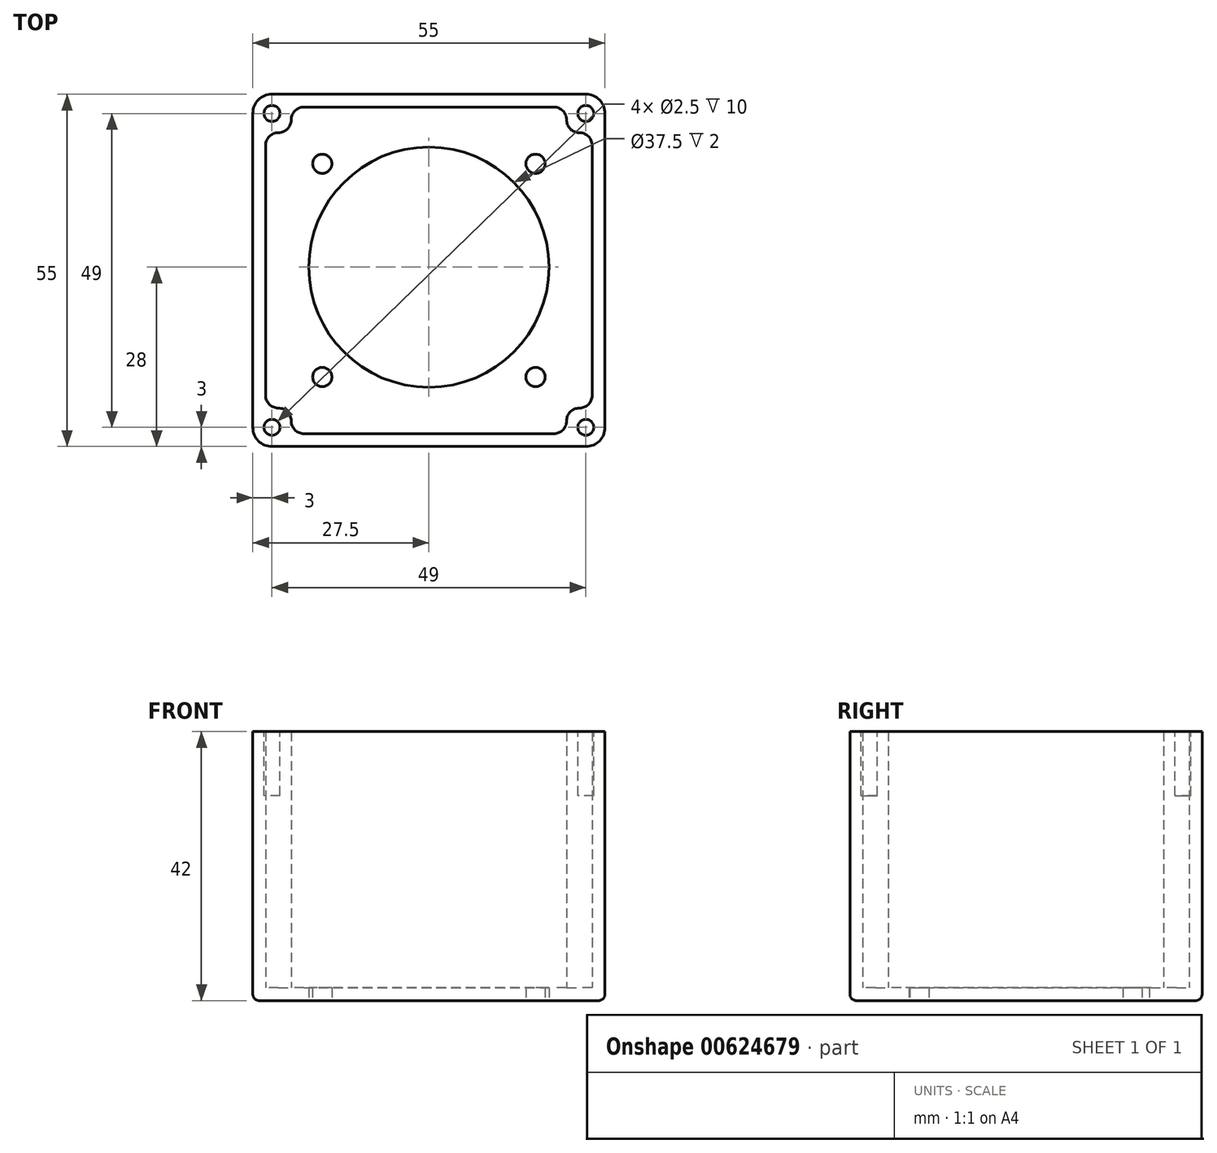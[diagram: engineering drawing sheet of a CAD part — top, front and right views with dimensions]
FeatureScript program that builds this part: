
annotation { "Feature Type Name" : "Feature", "Feature Type Description" : "" }
export const myFeature = defineFeature(function(context is Context, id is Id, definition is map)
    precondition{}
    {
        {
            var Q0;
            Q0=qCreatedBy(makeId("Top.planeOp"),FACE);
            var sketch = newSketch(context, id + "F0", { "sketchPlane" : qUnion([Q0])});
            skLineSegment(sketch, "E0.bottom", {"start": v(27.5, 27.5) * mm, "end": v(-27.5, 27.5) * mm});
            skLineSegment(sketch, "E0.top", {"start": v(27.5, -27.5) * mm, "end": v(-27.5, -27.5) * mm});
            skLineSegment(sketch, "E0.left", {"start": v(27.5, 27.5) * mm, "end": v(27.5, -27.5) * mm});
            skLineSegment(sketch, "E0.right", {"start": v(-27.5, 27.5) * mm, "end": v(-27.5, -27.5) * mm});
            skPoint(sketch, "E0.middle", {"position": v(0, 0) * mm});
            skCircle(sketch, "E1", {"center": v(0, 0.5) * mm, "radius": 18.75 * mm});
            skCircle(sketch, "E2", {"center": v(-16.65, 16.65) * mm, "radius": 1.5 * mm});
            skCircle(sketch, "E3", {"center": v(16.65, 16.65) * mm, "radius": 1.5 * mm});
            skCircle(sketch, "E4", {"center": v(16.65, -16.65) * mm, "radius": 1.5 * mm});
            skCircle(sketch, "E5", {"center": v(-16.65, -16.65) * mm, "radius": 1.5 * mm});
            skSolve(sketch);
        }
        {
            var Q0;
            Q0 = qSketchRegion(id + "F0", true);
            extrude(context, id + "F1", {"entities" : qUnion([Q0]), "depth" : 2 * mm, "offsetDistance" : 25 * mm});
        }
        {
            var Q0;
            Q0=makeQuery(id+"F1.opExtrude","CAP_FACE",FACE,{"disambiguationData":[OSD([sQuery(id+"F0.wireOp",EDGE,"E0.bottom"),sQuery(id+"F0.wireOp",EDGE,"E0.top"),sQuery(id+"F0.wireOp",EDGE,"E0.left"),sQuery(id+"F0.wireOp",EDGE,"E0.right"),sQuery(id+"F0.wireOp",EDGE,"E1"),sQuery(id+"F0.wireOp",EDGE,"E2"),sQuery(id+"F0.wireOp",EDGE,"E3"),sQuery(id+"F0.wireOp",EDGE,"E4"),sQuery(id+"F0.wireOp",EDGE,"E5")])],"isStart":false});
            var sketch = newSketch(context, id + "F2", { "sketchPlane" : qUnion([Q0])});
            skLineSegment(sketch, "E6.bottom", {"start": v(-27.5, 27.5) * mm, "end": v(27.5, 27.5) * mm});
            skLineSegment(sketch, "E6.top", {"start": v(-27.5, -27.5) * mm, "end": v(27.5, -27.5) * mm});
            skLineSegment(sketch, "E6.left", {"start": v(-27.5, 27.5) * mm, "end": v(-27.5, -27.5) * mm});
            skLineSegment(sketch, "E6.right", {"start": v(27.5, 27.5) * mm, "end": v(27.5, -27.5) * mm});
            skLineSegment(sketch, "E7.bottom", {"start": v(-21.5, 25.5) * mm, "end": v(21.5, 25.5) * mm});
            skLineSegment(sketch, "E7.top", {"start": v(-21.5, -25.5) * mm, "end": v(21.5, -25.5) * mm});
            skLineSegment(sketch, "E7.left", {"start": v(-25.5, 21.5) * mm, "end": v(-25.5, -21.5) * mm});
            skLineSegment(sketch, "E7.right", {"start": v(25.5, 21.5) * mm, "end": v(25.5, -21.5) * mm});
            skLineSegment(sketch, "E8.top", {"start": v(-25.5, 21.5) * mm, "end": v(-21.5, 21.5) * mm});
            skLineSegment(sketch, "E8.right", {"start": v(-21.5, 25.5) * mm, "end": v(-21.5, 21.5) * mm});
            skLineSegment(sketch, "E9.top", {"start": v(21.5, 21.5) * mm, "end": v(25.5, 21.5) * mm});
            skLineSegment(sketch, "E9.left", {"start": v(21.5, 25.5) * mm, "end": v(21.5, 21.5) * mm});
            skLineSegment(sketch, "E10.bottom", {"start": v(-25.5, -21.5) * mm, "end": v(-21.5, -21.5) * mm});
            skLineSegment(sketch, "E10.right", {"start": v(-21.5, -21.5) * mm, "end": v(-21.5, -25.5) * mm});
            skLineSegment(sketch, "E11.bottom", {"start": v(25.5, -21.5) * mm, "end": v(21.5, -21.5) * mm});
            skLineSegment(sketch, "E11.right", {"start": v(21.5, -21.5) * mm, "end": v(21.5, -25.5) * mm});
            skSolve(sketch);
        }
        {
            var Q0;
            Q0 = qSketchRegion(id + "F2", true);
            extrude(context, id + "F3", {"entities" : qUnion([Q0]), "operationType" : NewBodyOperationType.ADD, "depth" : 40 * mm, "offsetDistance" : 25 * mm});
        }
        {
            var Q0;
            Q0=makeQuery(id+"F3.opExtrude","CAP_FACE",FACE,{"disambiguationData":[OSD([sQuery(id+"F2.wireOp",EDGE,"E6.bottom"),sQuery(id+"F2.wireOp",EDGE,"E6.top"),sQuery(id+"F2.wireOp",EDGE,"E6.left"),sQuery(id+"F2.wireOp",EDGE,"E6.right"),sQuery(id+"F2.wireOp",EDGE,"E7.bottom"),sQuery(id+"F2.wireOp",EDGE,"E7.top"),sQuery(id+"F2.wireOp",EDGE,"E7.left"),sQuery(id+"F2.wireOp",EDGE,"E7.right"),sQuery(id+"F2.wireOp",EDGE,"E8.top"),sQuery(id+"F2.wireOp",EDGE,"E8.right"),sQuery(id+"F2.wireOp",EDGE,"E9.top"),sQuery(id+"F2.wireOp",EDGE,"E9.left"),sQuery(id+"F2.wireOp",EDGE,"E10.bottom"),sQuery(id+"F2.wireOp",EDGE,"E10.right"),sQuery(id+"F2.wireOp",EDGE,"E11.bottom"),sQuery(id+"F2.wireOp",EDGE,"E11.right")])],"isStart":false});
            var sketch = newSketch(context, id + "F4", { "sketchPlane" : qUnion([Q0])});
            skCircle(sketch, "E12", {"center": v(-24.5, 24.5) * mm, "radius": 1.25 * mm});
            skCircle(sketch, "E13.1.0", {"center": v(-24.5, -24.5) * mm, "radius": 1.25 * mm});
            skCircle(sketch, "E13.2.0", {"center": v(24.5, -24.5) * mm, "radius": 1.25 * mm});
            skCircle(sketch, "E13.3.0", {"center": v(24.5, 24.5) * mm, "radius": 1.25 * mm});
            skPoint(sketch, "E13.center", {"position": v(0, 0) * mm});
            skSolve(sketch);
        }
        {
            var Q0;
            Q0 = qSketchRegion(id + "F4", true);
            extrude(context, id + "F5", {"entities" : qUnion([Q0]), "operationType" : NewBodyOperationType.REMOVE, "oppositeDirection" : true, "depth" : 10 * mm, "offsetDistance" : 25 * mm});
        }
        {
            var Q0;
            Q0=makeQuery(id+"F3.boolean.opBoolean","MERGE",EDGE,{"derivedFrom":[makeQuery(id+"F1.opExtrude","SWEPT_EDGE",EDGE,{"disambiguationData":[OSD([sQuery(id+"F0.wireOp",EDGE,"E0.top"),sQuery(id+"F0.wireOp",EDGE,"E0.right")])]}),makeQuery(id+"F3.opExtrude","SWEPT_EDGE",EDGE,{"disambiguationData":[OSD([sQuery(id+"F2.wireOp",EDGE,"E6.top"),sQuery(id+"F2.wireOp",EDGE,"E6.left")])]})]});
            var Q1;
            Q1=makeQuery(id+"F3.boolean.opBoolean","MERGE",EDGE,{"derivedFrom":[makeQuery(id+"F1.opExtrude","SWEPT_EDGE",EDGE,{"disambiguationData":[OSD([sQuery(id+"F0.wireOp",EDGE,"E0.top"),sQuery(id+"F0.wireOp",EDGE,"E0.left")])]}),makeQuery(id+"F3.opExtrude","SWEPT_EDGE",EDGE,{"disambiguationData":[OSD([sQuery(id+"F2.wireOp",EDGE,"E6.top"),sQuery(id+"F2.wireOp",EDGE,"E6.right")])]})]});
            var Q2;
            Q2=makeQuery(id+"F3.boolean.opBoolean","MERGE",EDGE,{"derivedFrom":[makeQuery(id+"F1.opExtrude","SWEPT_EDGE",EDGE,{"disambiguationData":[OSD([sQuery(id+"F0.wireOp",EDGE,"E0.bottom"),sQuery(id+"F0.wireOp",EDGE,"E0.right")])]}),makeQuery(id+"F3.opExtrude","SWEPT_EDGE",EDGE,{"disambiguationData":[OSD([sQuery(id+"F2.wireOp",EDGE,"E6.bottom"),sQuery(id+"F2.wireOp",EDGE,"E6.left")])]})]});
            var Q3;
            Q3=makeQuery(id+"F3.boolean.opBoolean","MERGE",EDGE,{"derivedFrom":[makeQuery(id+"F1.opExtrude","SWEPT_EDGE",EDGE,{"disambiguationData":[OSD([sQuery(id+"F0.wireOp",EDGE,"E0.bottom"),sQuery(id+"F0.wireOp",EDGE,"E0.left")])]}),makeQuery(id+"F3.opExtrude","SWEPT_EDGE",EDGE,{"disambiguationData":[OSD([sQuery(id+"F2.wireOp",EDGE,"E6.bottom"),sQuery(id+"F2.wireOp",EDGE,"E6.right")])]})]});
            fillet(context, id + "F6", {"entities" : qUnion([Q0, Q1, Q2, Q3]), "radius" : 3 * mm, "tangentPropagation" : true, "allowEdgeOverflow" : false});
        }
        {
            var Q0;
            Q0=makeQuery(id+"F1.opExtrude","CAP_EDGE",EDGE,{"disambiguationData":[OSD([sQuery(id+"F0.wireOp",EDGE,"E0.top")])],"isStart":true});
            fillet(context, id + "F7", {"entities" : qUnion([Q0]), "radius" : 1 * mm, "tangentPropagation" : true, "allowEdgeOverflow" : false});
        }
        {
            var Q0;
            Q0=makeQuery(id+"F3.opExtrude","SWEPT_EDGE",EDGE,{"disambiguationData":[OSD([sQuery(id+"F2.wireOp",EDGE,"E11.bottom"),sQuery(id+"F2.wireOp",EDGE,"E11.right")])]});
            var Q1;
            Q1=makeQuery(id+"F3.opExtrude","SWEPT_EDGE",EDGE,{"disambiguationData":[OSD([sQuery(id+"F2.wireOp",EDGE,"E10.bottom"),sQuery(id+"F2.wireOp",EDGE,"E10.right")])]});
            var Q2;
            Q2=makeQuery(id+"F3.opExtrude","SWEPT_EDGE",EDGE,{"disambiguationData":[OSD([sQuery(id+"F2.wireOp",EDGE,"E7.top"),sQuery(id+"F2.wireOp",EDGE,"E10.right")])]});
            var Q3;
            Q3=makeQuery(id+"F3.opExtrude","SWEPT_EDGE",EDGE,{"disambiguationData":[OSD([sQuery(id+"F2.wireOp",EDGE,"E7.left"),sQuery(id+"F2.wireOp",EDGE,"E10.bottom")])]});
            var Q4;
            Q4=makeQuery(id+"F3.opExtrude","SWEPT_EDGE",EDGE,{"disambiguationData":[OSD([sQuery(id+"F2.wireOp",EDGE,"E7.top"),sQuery(id+"F2.wireOp",EDGE,"E11.right")])]});
            var Q5;
            Q5=makeQuery(id+"F3.opExtrude","SWEPT_EDGE",EDGE,{"disambiguationData":[OSD([sQuery(id+"F2.wireOp",EDGE,"E7.right"),sQuery(id+"F2.wireOp",EDGE,"E11.bottom")])]});
            var Q6;
            Q6=makeQuery(id+"F3.opExtrude","SWEPT_EDGE",EDGE,{"disambiguationData":[OSD([sQuery(id+"F2.wireOp",EDGE,"E8.top"),sQuery(id+"F2.wireOp",EDGE,"E8.right")])]});
            var Q7;
            Q7=makeQuery(id+"F3.opExtrude","SWEPT_EDGE",EDGE,{"disambiguationData":[OSD([sQuery(id+"F2.wireOp",EDGE,"E7.left"),sQuery(id+"F2.wireOp",EDGE,"E8.top")])]});
            var Q8;
            Q8=makeQuery(id+"F3.opExtrude","SWEPT_EDGE",EDGE,{"disambiguationData":[OSD([sQuery(id+"F2.wireOp",EDGE,"E7.bottom"),sQuery(id+"F2.wireOp",EDGE,"E8.right")])]});
            var Q9;
            Q9=makeQuery(id+"F3.opExtrude","SWEPT_EDGE",EDGE,{"disambiguationData":[OSD([sQuery(id+"F2.wireOp",EDGE,"E9.top"),sQuery(id+"F2.wireOp",EDGE,"E9.left")])]});
            var Q10;
            Q10=makeQuery(id+"F3.opExtrude","SWEPT_EDGE",EDGE,{"disambiguationData":[OSD([sQuery(id+"F2.wireOp",EDGE,"E7.bottom"),sQuery(id+"F2.wireOp",EDGE,"E9.left")])]});
            var Q11;
            Q11=makeQuery(id+"F3.opExtrude","SWEPT_EDGE",EDGE,{"disambiguationData":[OSD([sQuery(id+"F2.wireOp",EDGE,"E7.right"),sQuery(id+"F2.wireOp",EDGE,"E9.top")])]});
            var Q12;
            Q12=makeQuery(id+"F3.opExtrude","CAP_EDGE",EDGE,{"disambiguationData":[OSD([sQuery(id+"F2.wireOp",EDGE,"E7.top")])],"isStart":true});
            var Q13;
            Q13=makeQuery(id+"F3.opExtrude","CAP_EDGE",EDGE,{"disambiguationData":[OSD([sQuery(id+"F2.wireOp",EDGE,"E7.right")])],"isStart":true});
            var Q14;
            Q14=makeQuery(id+"F3.opExtrude","CAP_EDGE",EDGE,{"disambiguationData":[OSD([sQuery(id+"F2.wireOp",EDGE,"E7.left")])],"isStart":true});
            var Q15;
            Q15=makeQuery(id+"F3.opExtrude","CAP_EDGE",EDGE,{"disambiguationData":[OSD([sQuery(id+"F2.wireOp",EDGE,"E7.bottom")])],"isStart":true});
            var Q16;
            Q16=makeQuery(id+"F3.opExtrude","CAP_EDGE",EDGE,{"disambiguationData":[OSD([sQuery(id+"F2.wireOp",EDGE,"E10.bottom")])],"isStart":true});
            var Q17;
            Q17=makeQuery(id+"F3.opExtrude","CAP_EDGE",EDGE,{"disambiguationData":[OSD([sQuery(id+"F2.wireOp",EDGE,"E8.right")])],"isStart":true});
            var Q18;
            Q18=makeQuery(id+"F3.opExtrude","CAP_EDGE",EDGE,{"disambiguationData":[OSD([sQuery(id+"F2.wireOp",EDGE,"E11.right")])],"isStart":true});
            var Q19;
            Q19=makeQuery(id+"F3.opExtrude","CAP_EDGE",EDGE,{"disambiguationData":[OSD([sQuery(id+"F2.wireOp",EDGE,"E9.top")])],"isStart":true});
            fillet(context, id + "F8", {"entities" : qUnion([Q0, Q1, Q2, Q3, Q4, Q5, Q6, Q7, Q8, Q9, Q10, Q11, Q12, Q13, Q14, Q15, Q16, Q17, Q18, Q19]), "radius" : 2 * mm, "tangentPropagation" : true, "allowEdgeOverflow" : false});
        }
    });
